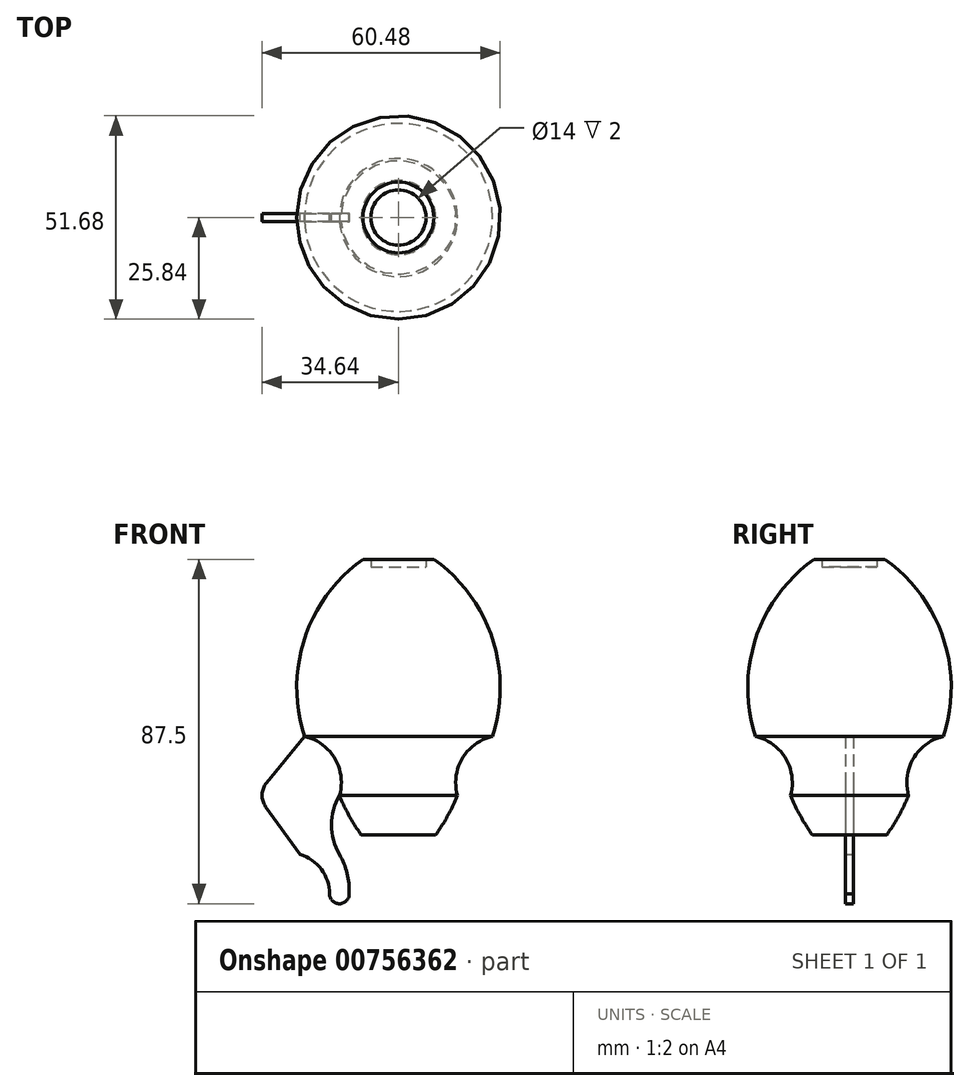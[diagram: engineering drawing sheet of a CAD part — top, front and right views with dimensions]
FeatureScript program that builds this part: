
annotation { "Feature Type Name" : "Feature", "Feature Type Description" : "" }
export const myFeature = defineFeature(function(context is Context, id is Id, definition is map)
    precondition{}
    {
        {
            var Q0;
            Q0=qCreatedBy(makeId("Front.planeOp"),FACE);
            var sketch = newSketch(context, id + "F0", { "sketchPlane" : qUnion([Q0])});
            skLineSegment(sketch, "E0", {"start": v(0, 0) * mm, "end": v(0, 80) * mm});
            skLineSegment(sketch, "E1", {"start": v(0, 35) * mm, "end": v(23.88, 35) * mm});
            skLineSegment(sketch, "E2", {"start": v(0, 80) * mm, "end": v(9, 80) * mm});
            skLineSegment(sketch, "E3", {"start": v(0, 20) * mm, "end": v(15, 20) * mm});
            skArc(sketch, "E4", {"start": v(23.88, 35) * mm, "mid": v(23.82, 59.94) * mm, "end": v(9, 80) * mm});
            skArc(sketch, "E5", {"start": v(23.88, 35) * mm, "mid": v(16.21, 29.41) * mm, "end": v(15, 20) * mm});
            skArc(sketch, "E6", {"start": v(0, 0) * mm, "mid": v(8.77, 9.05) * mm, "end": v(15, 20) * mm});
            skLineSegment(sketch, "E7", {"start": v(7, 80) * mm, "end": v(7, 78) * mm});
            skLineSegment(sketch, "E8", {"start": v(7, 78) * mm, "end": v(0, 78) * mm});
            skSolve(sketch);
        }
        {
            var Q0;
            {var subQ2=sQuery(id+"F0.wireOp",EDGE,"E3");Q0=makeQuery(id+"F0.imprint","IMPRINT",FACE,{"disambiguationData":[TD([[makeQuery(id+"F0.imprint","IMPRINT",EDGE,{"derivedFrom":subQ2}),-1.0]])]});}
            var Q1;
            {var subQ0=sQuery(id+"F0.wireOp",EDGE,"E1");Q1=makeQuery(id+"F0.imprint","IMPRINT",FACE,{"disambiguationData":[TD([[makeQuery(id+"F0.imprint","IMPRINT",EDGE,{"derivedFrom":subQ0}),-1.0]])]});}
            var Q2;
            {var subQ3=sQuery(id+"F0.wireOp",EDGE,"E1");Q2=makeQuery(id+"F0.imprint","IMPRINT",FACE,{"disambiguationData":[TD([[makeQuery(id+"F0.imprint","IMPRINT",EDGE,{"derivedFrom":subQ3}),1.0]])]});}
            var Q3;
            Q3=sQuery(id+"F0.wireOp",EDGE,"E0");
            revolve(context, id + "F1", {"surfaceOperationType" : NewSurfaceOperationType.NEW, "entities" : qUnion([Q0, Q1, Q2]), "axis" : qUnion([Q3]), "revolveType" : RevolveType.FULL});
        }
        {
            var Q0;
            Q0=qCreatedBy(makeId("Front.planeOp"),FACE);
            var sketch = newSketch(context, id + "F2", { "sketchPlane" : qUnion([Q0])});
            skArc(sketch, "E9", {"start": v(-15, 20) * mm, "mid": v(-16.21, 29.41) * mm, "end": v(-23.88, 35) * mm});
            skLineSegment(sketch, "E10.0", {"start": v(23.88, 35) * mm, "end": v(-23.88, 35) * mm});
            skLineSegment(sketch, "E11.0", {"start": v(15, 20) * mm, "end": v(-15, 20) * mm});
            skLineSegment(sketch, "E12", {"start": v(-23.88, 35) * mm, "end": v(-15, 20) * mm});
            skLineSegment(sketch, "E13", {"start": v(-23.88, 35) * mm, "end": v(0, 35) * mm});
            skLineSegment(sketch, "E14", {"start": v(0, 35) * mm, "end": v(0, 20) * mm});
            skLineSegment(sketch, "E15", {"start": v(0, 20) * mm, "end": v(-15, 20) * mm});
            skSolve(sketch);
        }
        {
            var Q0;
            Q0 = qSketchRegion(id + "F2", true);
            extrude(context, id + "F3", {"entities" : qUnion([Q0]), "operationType" : NewBodyOperationType.ADD, "endBound" : BoundingType.SYMMETRIC, "depth" : 2 * mm, "offsetDistance" : 25 * mm});
        }
        {
            var Q0;
            Q0=qCreatedBy(makeId("Front.planeOp"),FACE);
            var sketch = newSketch(context, id + "F4", { "sketchPlane" : qUnion([Q0])});
            skLineSegment(sketch, "E16", {"start": v(0, 0) * mm, "end": v(0, -5) * mm});
            skLineSegment(sketch, "E17", {"start": v(0, -5) * mm, "end": v(-15, -5) * mm});
            skLineSegment(sketch, "E18", {"start": v(-15, -5) * mm, "end": v(-15, 5) * mm});
            skLineSegment(sketch, "E19", {"start": v(-15, 5) * mm, "end": v(-25, 5) * mm});
            skArc(sketch, "E20", {"start": v(-17.5, -5) * mm, "mid": v(-15, -7.5) * mm, "end": v(-12.5, -5) * mm});
            skLineSegment(sketch, "E21", {"start": v(-15, -5) * mm, "end": v(-17.5, -5) * mm});
            skFitSpline(sketch, "E22.0", {"points": [v(-23.86, 35) * mm, v(-23.46, 34.91) * mm, v(-22.67, 34.69) * mm, v(-21.54, 34.24) * mm, v(-20.46, 33.68) * mm, v(-19.6, 33.13) * mm, v(-18.96, 32.63) * mm, v(-18.34, 32.1) * mm, v(-17.62, 31.39) * mm, v(-16.85, 30.45) * mm, v(-16.16, 29.42) * mm, v(-15.6, 28.35) * mm, v(-15.22, 27.4) * mm, v(-14.97, 26.63) * mm, v(-14.76, 25.84) * mm, v(-14.62, 25.04) * mm, v(-14.53, 24.22) * mm, v(-14.5, 23.4) * mm, v(-14.53, 21.98) * mm, v(-14.74, 20.79) * mm, v(-14.97, 20) * mm]});
            skArc(sketch, "E23", {"start": v(-14.97, 20) * mm, "mid": v(-17, 12.5) * mm, "end": v(-15, 5) * mm});
            skArc(sketch, "E24", {"start": v(-12.5, -5) * mm, "mid": v(-13.05, 0.17) * mm, "end": v(-15, 5) * mm});
            skArc(sketch, "E25", {"start": v(-17.5, -5) * mm, "mid": v(-19.58, 1.25) * mm, "end": v(-25, 5) * mm});
            skLineSegment(sketch, "E26", {"start": v(-23.86, 35) * mm, "end": v(-33.5, 23.24) * mm});
            skLineSegment(sketch, "E27", {"start": v(-33.7, 17.16) * mm, "end": v(-25, 5) * mm});
            skPoint(sketch, "E28.visualSharp", {"position": v(-35.94, 20.27) * mm});
            skArc(sketch, "E28.filletArc", {"start": v(-33.5, 23.24) * mm, "mid": v(-34.64, 20.23) * mm, "end": v(-33.7, 17.16) * mm});
            skSolve(sketch);
        }
        {
            var Q0;
            Q0 = qSketchRegion(id + "F4", true);
            extrude(context, id + "F5", {"entities" : qUnion([Q0]), "operationType" : NewBodyOperationType.ADD, "endBound" : BoundingType.SYMMETRIC, "depth" : 2 * mm, "offsetDistance" : 25 * mm});
        }
        {
            var Q0;
            Q0=qCreatedBy(makeId("Top.planeOp"),FACE);
            var sketch = newSketch(context, id + "F6", { "sketchPlane" : qUnion([Q0])});
            skCircle(sketch, "E29", {"center": v(0, 0) * mm, "radius": 10 * mm});
            skSolve(sketch);
        }
        {
            var Q0;
            Q0 = qSketchRegion(id + "F6", true);
            extrude(context, id + "F7", {"entities" : qUnion([Q0]), "operationType" : NewBodyOperationType.REMOVE, "endBound" : BoundingType.SYMMETRIC, "oppositeDirection" : true, "depth" : 20 * mm, "offsetDistance" : 25 * mm});
        }
    });
